# Revit family: Zahnplatte S, VA
name_source: partatom
category: HLS-Bauteile
revit_build: Autodesk Revit 2017 (Build: 20190507_1515(x64)
units: mm (PartAtom-declared; Revit-internal decimal feet)

## family parameters
Arbeitsebenenbasiert = Ja
Beim Laden mit Abzugskörper schneiden = Nein
Bemaßung runder Anschluss = Durchmesser verwenden
Gemeinsam genutzt = Ja
Immer vertikal = Nein
Raumberechnungspunkt = Nein
Teiletyp = Normal

## types (3) — shared parameters
B = 38 mm  [stored 0.124672 ft]
Fabrikat = MEFA
Kurztext1 = Zahnplatte S V4A
Material = Edelstahl
S = 9 mm  [stored 0.0295276 ft]
Vorgabe-Ansicht = 1219 mm

## per-type parameters (varying)
| type | Artikelnummer | EAN | Gewicht | Gewicht pro Bauteil | Kurztext2 | d2 |
| Zahnplatte S M10, A4 | 0481616 | 4250928459350 | 0.05 kg | 0.05 kg | M10 36 x 20 mm | 4 mm  [stored 0.0131234 ft] |
| Zahnplatte S M 8, A4 | 0481615 | 4250928459343 | 0.05 kg | 0.05 kg | M8 36 x 20 mm | 3 mm  [stored 0.00984252 ft] |
| Zahnplatte S M12, A4 | 0481617 | 4250928459367 | 0.04 kg | 0.04 kg | M12 36 x 20 mm | 5 mm  [stored 0.0164042 ft] |

note: [stored X ft] marks values corroborated as IEEE doubles in the binary element streams (Revit-internal decimal feet)
